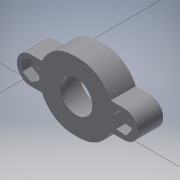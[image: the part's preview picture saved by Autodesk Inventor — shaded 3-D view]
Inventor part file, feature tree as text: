
AUTODESK INVENTOR PART (.ipt)
format: ipt  version: 2019 (Build 230136000, 136)  size: 216,064 bytes
history: native  units: mm
features: other x4, extrude x4, sketch x4, reference x3, fillet x2, projected_geometry x2
ambient origin geometry x8: Origin, YZ Plane, XZ Plane, XY Plane, X Axis, Y Axis, Z Axis, Center Point
bodies: Body1 (feature_tree)
feature tree (19):
  other  "Твердое тело1"
  extrude  "Выдавливание1"  Depth=15.0mm
  fillet  "Сопряжение1"  Radius=15.0mm
  fillet  "Сопряжение2"  Radius=15.0mm
  extrude  "Выдавливание2"  Depth=15.0mm
  extrude  "Выдавливание3"  Depth=6.0mm
  extrude  "Выдавливание4"  Depth=6.0mm
  sketch  "Эскиз1"
  reference  "Ссылка1"
  reference  "Ссылка2"
  reference  "Ссылка3"
  sketch  "Эскиз2"
  projected_geometry  "Спроецированная петля1"
  sketch  "Эскиз3"
  projected_geometry  "Спроецированная петля2"
  sketch  "Эскиз4"
  parser-record x1  (decoder bookkeeping rows leaked as tree rows — omitted from the tree; the rows remain in map.json)
  other  "kowsh.iam"
  other  "боковушка:1"
note: 1 file-system path scrubbed to <path> (originals preserved in map.json)
